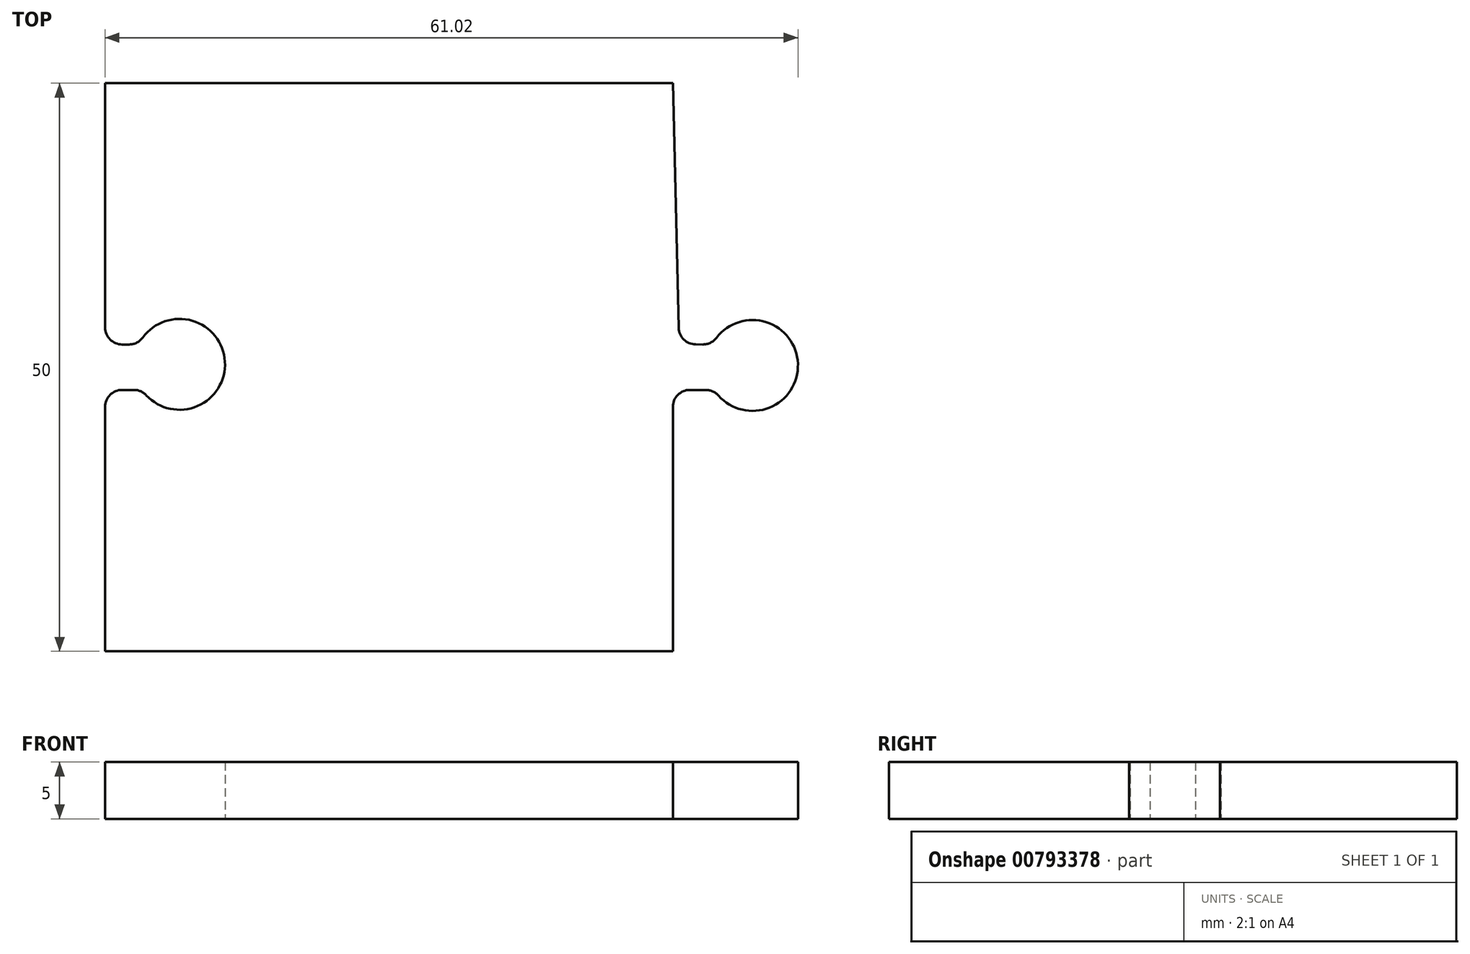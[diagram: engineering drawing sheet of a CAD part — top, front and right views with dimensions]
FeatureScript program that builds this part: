
annotation { "Feature Type Name" : "Feature", "Feature Type Description" : "" }
export const myFeature = defineFeature(function(context is Context, id is Id, definition is map)
    precondition{}
    {
        {
            var Q0;
            Q0=qCreatedBy(makeId("Top.planeOp"),FACE);
            var sketch = newSketch(context, id + "F0", { "sketchPlane" : qUnion([Q0])});
            skLineSegment(sketch, "E0", {"start": v(21.12, 25.04) * mm, "end": v(-28.88, 25.04) * mm});
            skLineSegment(sketch, "E1", {"start": v(-28.88, 25.04) * mm, "end": v(-28.88, 3.54) * mm});
            skLineSegment(sketch, "E2", {"start": v(21.12, -24.96) * mm, "end": v(-28.88, -24.96) * mm});
            skLineSegment(sketch, "E3", {"start": v(-28.88, -24.96) * mm, "end": v(-28.88, -3.46) * mm});
            skLineSegment(sketch, "E4", {"start": v(-27.38, -1.96) * mm, "end": v(-26.34, -1.96) * mm});
            skLineSegment(sketch, "E5", {"start": v(-27.38, 2.04) * mm, "end": v(-26.75, 2.04) * mm});
            skPoint(sketch, "E6.visualSharp", {"position": v(-28.88, 2.04) * mm});
            skArc(sketch, "E6.filletArc", {"start": v(-28.88, 3.54) * mm, "mid": v(-28.44, 2.48) * mm, "end": v(-27.38, 2.04) * mm});
            skPoint(sketch, "E7.visualSharp", {"position": v(-28.88, -1.96) * mm});
            skArc(sketch, "E7.filletArc", {"start": v(-27.38, -1.96) * mm, "mid": v(-28.44, -2.4) * mm, "end": v(-28.88, -3.46) * mm});
            skArc(sketch, "E8", {"start": v(-25.24, -2.43) * mm, "mid": v(-18.32, 0.53) * mm, "end": v(-25.54, 2.66) * mm});
            skLineSegment(sketch, "E9.trimOffspring", {"start": v(-20.6, -1.96) * mm, "end": v(-18.42, -1.96) * mm});
            skLineSegment(sketch, "E10.trimOffspring", {"start": v(-18.72, 2.04) * mm, "end": v(-18.42, 2.04) * mm});
            skPoint(sketch, "E11.visualSharp", {"position": v(-25.62, -1.96) * mm});
            skArc(sketch, "E11.filletArc", {"start": v(-25.24, -2.43) * mm, "mid": v(-25.74, -2.08) * mm, "end": v(-26.34, -1.96) * mm});
            skPoint(sketch, "E12.visualSharp", {"position": v(-25.91, 2.04) * mm});
            skArc(sketch, "E12.filletArc", {"start": v(-26.75, 2.04) * mm, "mid": v(-26.08, 2.2) * mm, "end": v(-25.54, 2.66) * mm});
            skPoint(sketch, "E13.end.orphan", {"position": v(31.57, 2.02) * mm});
            skPoint(sketch, "E14.end.orphan", {"position": v(31.57, -1.96) * mm});
            skLineSegment(sketch, "E15", {"start": v(21.12, 25.04) * mm, "end": v(21.64, 3.5) * mm});
            skLineSegment(sketch, "E16", {"start": v(21.12, -24.96) * mm, "end": v(21.12, -3.46) * mm});
            skLineSegment(sketch, "E17", {"start": v(22.62, -1.96) * mm, "end": v(24.02, -1.96) * mm});
            skLineSegment(sketch, "E18", {"start": v(23.14, 2.05) * mm, "end": v(23.77, 2.04) * mm});
            skArc(sketch, "E19", {"start": v(25.14, -2.46) * mm, "mid": v(32.13, 0.34) * mm, "end": v(24.96, 2.63) * mm});
            skLineSegment(sketch, "E20.trimOffspring", {"start": v(31.5, -1.96) * mm, "end": v(31.57, -1.96) * mm});
            skPoint(sketch, "E21.visualSharp", {"position": v(21.68, 2.05) * mm});
            skArc(sketch, "E21.filletArc", {"start": v(21.64, 3.5) * mm, "mid": v(22.1, 2.47) * mm, "end": v(23.14, 2.05) * mm});
            skPoint(sketch, "E22.visualSharp", {"position": v(21.12, -1.96) * mm});
            skArc(sketch, "E22.filletArc", {"start": v(22.62, -1.96) * mm, "mid": v(21.56, -2.4) * mm, "end": v(21.12, -3.46) * mm});
            skPoint(sketch, "E23.visualSharp", {"position": v(24.59, 2.04) * mm});
            skArc(sketch, "E23.filletArc", {"start": v(23.77, 2.04) * mm, "mid": v(24.44, 2.2) * mm, "end": v(24.96, 2.63) * mm});
            skPoint(sketch, "E24.visualSharp", {"position": v(24.76, -1.96) * mm});
            skArc(sketch, "E24.filletArc", {"start": v(25.14, -2.46) * mm, "mid": v(24.64, -2.09) * mm, "end": v(24.02, -1.96) * mm});
            skSolve(sketch);
        }
        {
            var Q0;
            Q0 = qSketchRegion(id + "F0", true);
            extrude(context, id + "F1", {"entities" : qUnion([Q0]), "depth" : 5 * mm, "offsetDistance" : 25 * mm});
        }
    });
